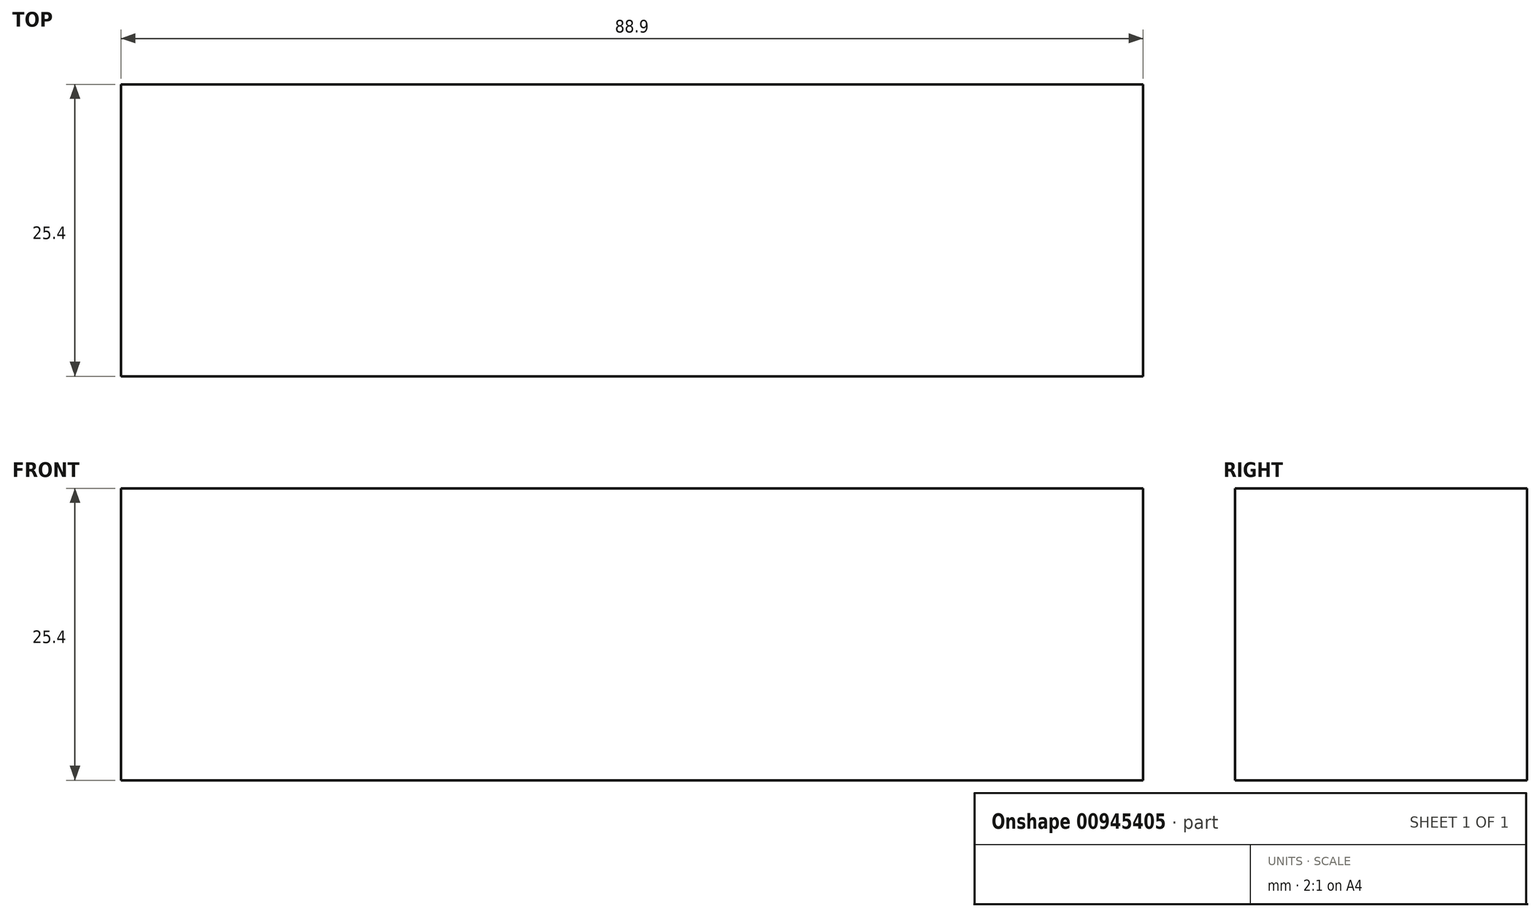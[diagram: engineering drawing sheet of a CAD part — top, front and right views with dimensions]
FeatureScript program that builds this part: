
annotation { "Feature Type Name" : "Feature", "Feature Type Description" : "" }
export const myFeature = defineFeature(function(context is Context, id is Id, definition is map)
    precondition{}
    {
        {
            var Q0;
            Q0=qCreatedBy(makeId("Right.planeOp"),FACE);
            var sketch = newSketch(context, id + "F0", { "sketchPlane" : qUnion([Q0])});
            skLineSegment(sketch, "E0.bottom", {"start": v(26.29, -16) * mm, "end": v(51.69, -16) * mm});
            skLineSegment(sketch, "E0.top", {"start": v(26.29, -41.4) * mm, "end": v(51.69, -41.4) * mm});
            skLineSegment(sketch, "E0.left", {"start": v(26.29, -16) * mm, "end": v(26.29, -41.4) * mm});
            skLineSegment(sketch, "E0.right", {"start": v(51.69, -16) * mm, "end": v(51.69, -41.4) * mm});
            skSolve(sketch);
        }
        {
            var Q0;
            Q0=makeQuery(id+"F0.imprint","IMPRINT",FACE,{"disambiguationData":[TD([[makeQuery(id+"F0.imprint","IMPRINT",EDGE,{"derivedFrom":sQuery(id+"F0.wireOp",EDGE,"E0.bottom")}),-1.0]])]});
            var Q1;
            Q1=sQuery(id+"F0.wireOp",EDGE,"E0.bottom");
            var Q2;
            Q2=sQuery(id+"F0.wireOp",EDGE,"E0.left");
            var Q3;
            Q3=sQuery(id+"F0.wireOp",EDGE,"E0.right");
            var Q4;
            Q4=sQuery(id+"F0.wireOp",EDGE,"E0.top");
            extrude(context, id + "F1", {"entities" : qUnion([Q0]), "bodyType" : ToolBodyType.SURFACE, "surfaceEntities" : qUnion([Q1, Q2, Q3, Q4]), "depth" : 88.9 * mm, "offsetDistance" : 25.4 * mm});
        }
    });
